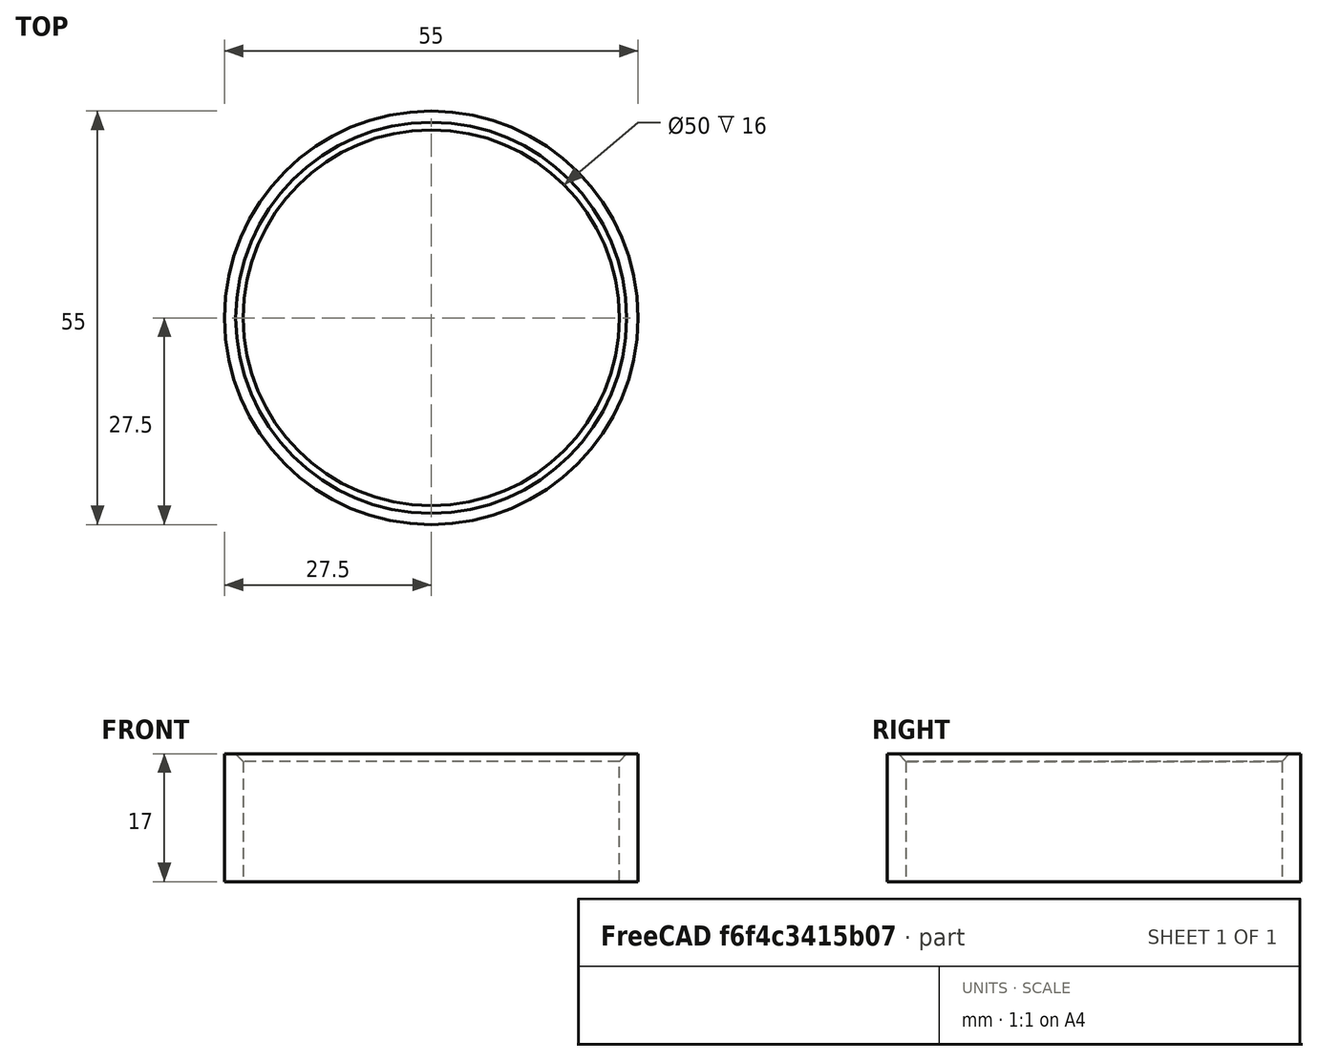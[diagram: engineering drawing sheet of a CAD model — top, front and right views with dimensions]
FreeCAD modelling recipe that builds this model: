
FCSTD DOCUMENT  (FreeCAD 0.19R24276 (Git))
Label: Stopper
License: All rights reserved
LicenseURL: http://en.wikipedia.org/wiki/All_rights_reserved
objects: Sketcher::SketchObject×1, PartDesign::Pad×1, PartDesign::Chamfer×1, PartDesign::Body×1
note: 6 computed .brp shape members not serialized (recipe doc carries the construction recipe); baked Part::Feature solids carry a one-line shape summary decoded from their .brp

FEATURE [Sketcher::SketchObject] Sketch  label="Sketch_d50_d55"
  FullyConstrained = true
  MapMode = 5
  Support = -> [XY_Plane]
  sketch-geometry (2):
    g0: Circle CenterX=0 CenterY=0 CenterZ=0 NormalX=0 NormalY=0 NormalZ=1 AngleXU=0 Radius=25
    g1: Circle CenterX=0 CenterY=0 CenterZ=0 NormalX=0 NormalY=0 NormalZ=1 AngleXU=0 Radius=27.5
  constraints (4):
    c: Coincident(g0,g-1)
    c: Coincident(g1,g0)
    c: Diameter(g0) = 50
    c: Diameter(g1) = 55
FEATURE [PartDesign::Pad] Pad  label="Pad_h17"
  Direction = (1,1,1)
  Length = 17
  Length2 = 100
  Profile = -> Sketch
  Type = 0
FEATURE [PartDesign::Chamfer] Chamfer
  Angle = 45
  Base = -> Pad [Edge6]
  BaseFeature = -> Pad
  ChamferType = 0
  FlipDirection = false
  Size = 1
  Size2 = 1
  SupportTransform = false
FEATURE [PartDesign::Body] Body
  Group = -> [Sketch,Pad,Chamfer]
  Origin = -> Origin
  Tip = -> Chamfer
